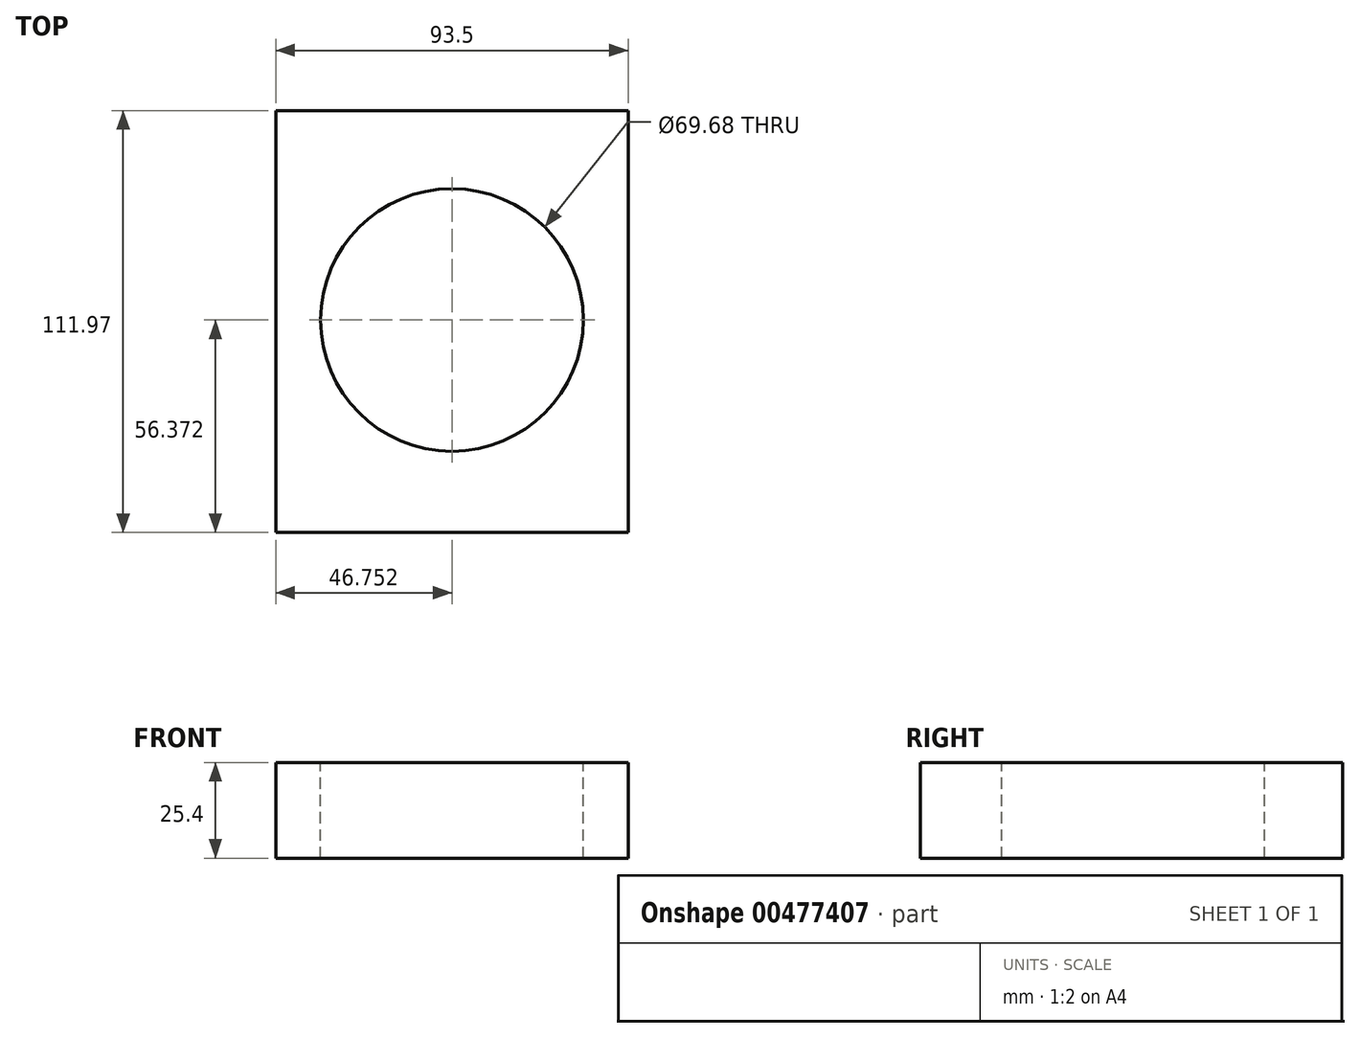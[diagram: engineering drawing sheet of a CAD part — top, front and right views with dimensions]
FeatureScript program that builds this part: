
annotation { "Feature Type Name" : "Feature", "Feature Type Description" : "" }
export const myFeature = defineFeature(function(context is Context, id is Id, definition is map)
    precondition{}
    {
        {
            var Q0;
            Q0=qCreatedBy(makeId("Top.planeOp"),FACE);
            var sketch = newSketch(context, id + "F0", { "sketchPlane" : qUnion([Q0])});
            skLineSegment(sketch, "E0.bottom", {"start": v(0, 0) * mm, "end": v(-93.5, 0) * mm});
            skLineSegment(sketch, "E0.top", {"start": v(0, -111.97) * mm, "end": v(-93.5, -111.97) * mm});
            skLineSegment(sketch, "E0.left", {"start": v(0, 0) * mm, "end": v(0, -111.97) * mm});
            skLineSegment(sketch, "E0.right", {"start": v(-93.5, 0) * mm, "end": v(-93.5, -111.97) * mm});
            skSolve(sketch);
        }
        {
            var Q0;
            Q0=makeQuery(id+"F0.imprint","IMPRINT",FACE,{"disambiguationData":[TD([[makeQuery(id+"F0.imprint","IMPRINT",EDGE,{"derivedFrom":sQuery(id+"F0.wireOp",EDGE,"E0.bottom")}),1.0]])]});
            extrude(context, id + "F1", {"entities" : qUnion([Q0]), "depth" : 25.4 * mm});
        }
        {
            var Q0;
            Q0=makeQuery(id+"F1.opExtrude","CAP_FACE",FACE,{"disambiguationData":[OSD([sQuery(id+"F0.wireOp",EDGE,"E0.bottom"),sQuery(id+"F0.wireOp",EDGE,"E0.top"),sQuery(id+"F0.wireOp",EDGE,"E0.left"),sQuery(id+"F0.wireOp",EDGE,"E0.right")])],"isStart":false});
            var sketch = newSketch(context, id + "F2", { "sketchPlane" : qUnion([Q0])});
            skCircle(sketch, "E1", {"center": v(-46.75, -55.6) * mm, "radius": 34.84 * mm});
            skPoint(sketch, "E1.centerSnap0", {"position": v(-46.75, 0) * mm});
            skSolve(sketch);
        }
        {
            var Q0;
            Q0=makeQuery(id+"F2.imprint","IMPRINT",FACE,{"disambiguationData":[TD([[makeQuery(id+"F2.imprint","IMPRINT",EDGE,{"derivedFrom":sQuery(id+"F2.wireOp",EDGE,"E1")}),1.0]])]});
            extrude(context, id + "F3", {"entities" : qUnion([Q0]), "operationType" : NewBodyOperationType.REMOVE, "oppositeDirection" : true, "depth" : 65.1 * mm});
        }
    });
